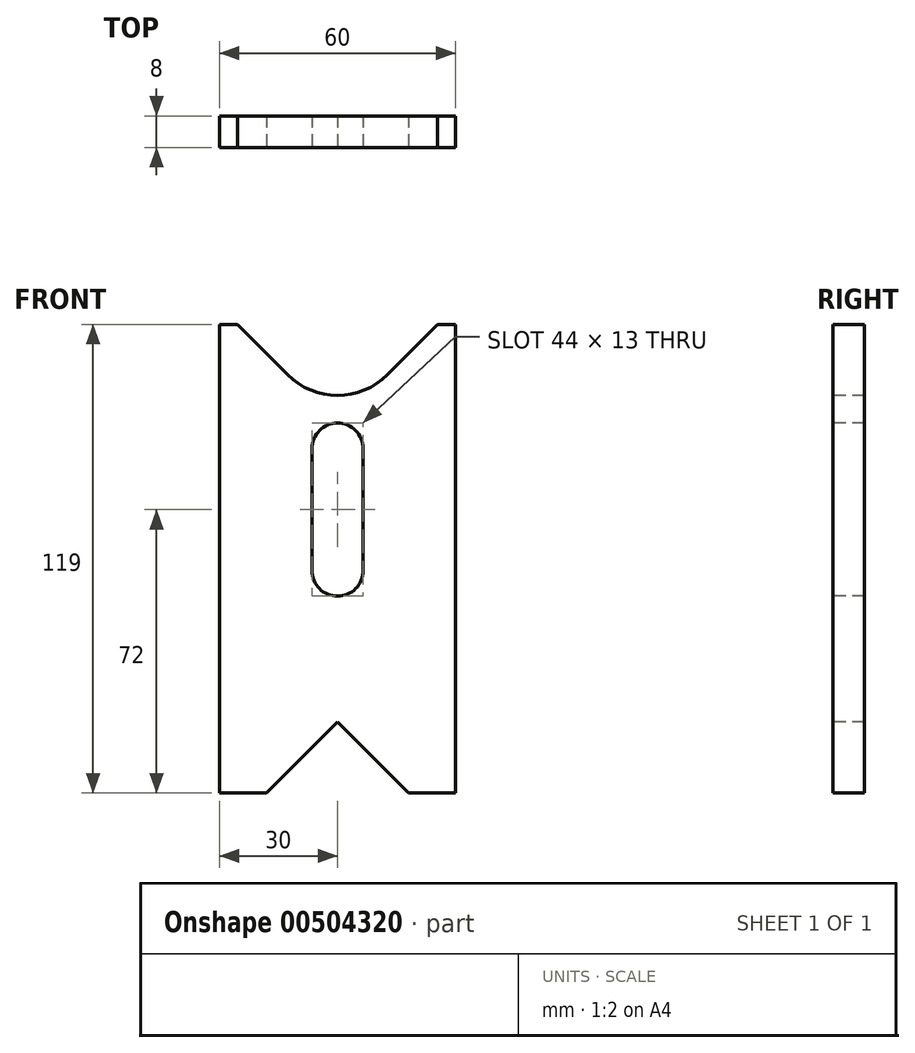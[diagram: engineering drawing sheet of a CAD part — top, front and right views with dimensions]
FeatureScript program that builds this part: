
annotation { "Feature Type Name" : "Feature", "Feature Type Description" : "" }
export const myFeature = defineFeature(function(context is Context, id is Id, definition is map)
    precondition{}
    {
        {
            var Q0;
            Q0=qCreatedBy(makeId("Front.planeOp"),FACE);
            var sketch = newSketch(context, id + "F0", { "sketchPlane" : qUnion([Q0])});
            skLineSegment(sketch, "E0.bottom", {"start": v(30, 59.5) * mm, "end": v(-30, 59.5) * mm});
            skLineSegment(sketch, "E0.top", {"start": v(30, -59.5) * mm, "end": v(-30, -59.5) * mm});
            skLineSegment(sketch, "E0.left", {"start": v(30, 59.5) * mm, "end": v(30, -59.5) * mm});
            skLineSegment(sketch, "E0.right", {"start": v(-30, 59.5) * mm, "end": v(-30, -59.5) * mm});
            skPoint(sketch, "E0.middle", {"position": v(0, 0) * mm});
            skSolve(sketch);
        }
        {
            var Q0;
            Q0 = qSketchRegion(id + "F0", true);
            extrude(context, id + "F1", {"entities" : qUnion([Q0]), "depth" : 8 * mm});
        }
        {
            var Q0;
            Q0=makeQuery(id+"F1.opExtrude","CAP_FACE",FACE,{"disambiguationData":[OSD([sQuery(id+"F0.wireOp",EDGE,"E0.bottom"),sQuery(id+"F0.wireOp",EDGE,"E0.top"),sQuery(id+"F0.wireOp",EDGE,"E0.left"),sQuery(id+"F0.wireOp",EDGE,"E0.right")])],"isStart":false});
            var sketch = newSketch(context, id + "F2", { "sketchPlane" : qUnion([Q0])});
            skLineSegment(sketch, "E1", {"start": v(0, 28) * mm, "end": v(0, -3) * mm, "construction": true});
            skArc(sketch, "E2.0.startCap", {"start": v(-6.5, 28) * mm, "mid": v(0, 34.5) * mm, "end": v(6.5, 28) * mm});
            skArc(sketch, "E2.0.endCap", {"start": v(6.5, -3) * mm, "mid": v(0, -9.5) * mm, "end": v(-6.5, -3) * mm});
            skLineSegment(sketch, "E2.0.left", {"start": v(6.5, 28) * mm, "end": v(6.5, -3) * mm});
            skLineSegment(sketch, "E2.0.right", {"start": v(-6.5, 28) * mm, "end": v(-6.5, -3) * mm});
            skArc(sketch, "E3", {"start": v(-12.73, 46.77) * mm, "mid": v(0, 41.5) * mm, "end": v(12.73, 46.77) * mm});
            skLineSegment(sketch, "E4", {"start": v(12.73, 46.77) * mm, "end": v(25.46, 59.5) * mm});
            skLineSegment(sketch, "E5.MirrorCS", {"start": v(-12.73, 46.77) * mm, "end": v(-25.46, 59.5) * mm});
            skLineSegment(sketch, "E6.0", {"start": v(25.46, 59.5) * mm, "end": v(-25.46, 59.5) * mm});
            skPoint(sketch, "E7.orphan", {"position": v(-30, 59.5) * mm});
            skPoint(sketch, "E8.orphan", {"position": v(30, 59.5) * mm});
            skLineSegment(sketch, "E9", {"start": v(0, -59.5) * mm, "end": v(0, -41.5) * mm, "construction": true});
            skLineSegment(sketch, "E10", {"start": v(0, -41.5) * mm, "end": v(18, -59.5) * mm});
            skLineSegment(sketch, "E11.MirrorCS", {"start": v(0, -41.5) * mm, "end": v(-18, -59.5) * mm});
            skLineSegment(sketch, "E12.0", {"start": v(18, -59.5) * mm, "end": v(-18, -59.5) * mm});
            skPoint(sketch, "E13.orphan", {"position": v(30, -59.5) * mm});
            skPoint(sketch, "E14.orphan", {"position": v(-30, -59.5) * mm});
            skSolve(sketch);
        }
        {
            var Q0;
            Q0 = qSketchRegion(id + "F2", true);
            extrude(context, id + "F3", {"entities" : qUnion([Q0]), "operationType" : NewBodyOperationType.REMOVE, "endBound" : BoundingType.THROUGH_ALL, "oppositeDirection" : true, "depth" : 25 * mm});
        }
    });
